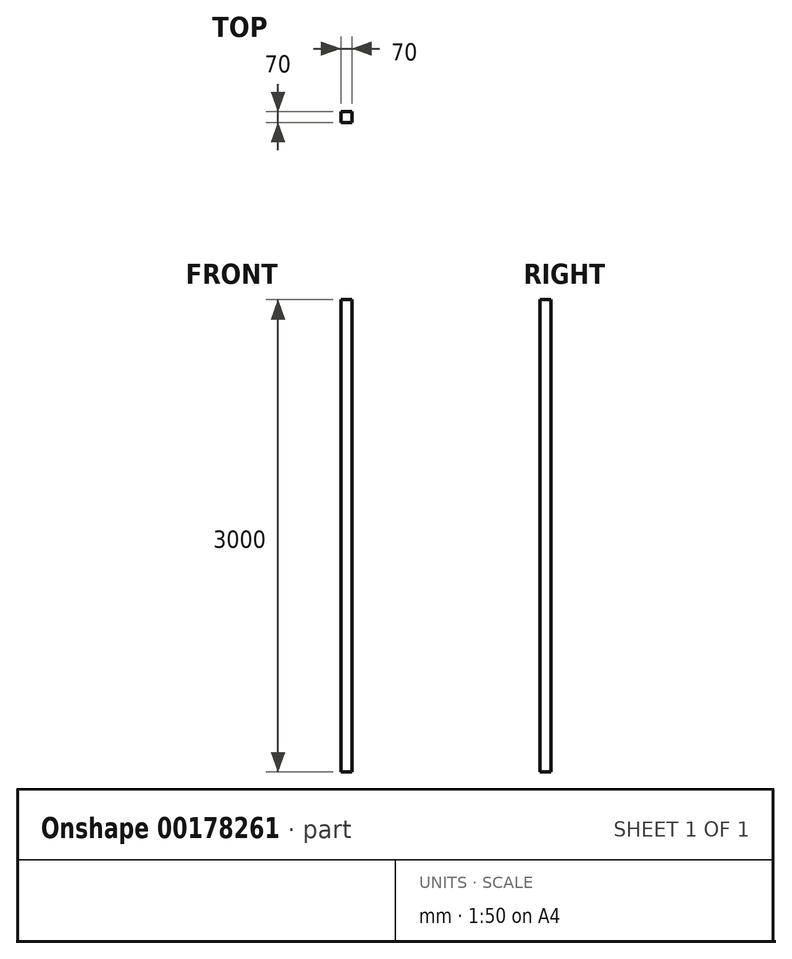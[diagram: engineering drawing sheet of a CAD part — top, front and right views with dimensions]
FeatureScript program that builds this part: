
annotation { "Feature Type Name" : "Feature", "Feature Type Description" : "" }
export const myFeature = defineFeature(function(context is Context, id is Id, definition is map)
    precondition{}
    {
        {
            var Q0;
            Q0=qCreatedBy(makeId("Top.planeOp"),FACE);
            var sketch = newSketch(context, id + "F0", { "sketchPlane" : qUnion([Q0])});
            skLineSegment(sketch, "E0.bottom", {"start": v(-35, -35) * mm, "end": v(35, -35) * mm});
            skLineSegment(sketch, "E0.top", {"start": v(-35, 35) * mm, "end": v(35, 35) * mm});
            skLineSegment(sketch, "E0.left", {"start": v(-35, -35) * mm, "end": v(-35, 35) * mm});
            skLineSegment(sketch, "E0.right", {"start": v(35, -35) * mm, "end": v(35, 35) * mm});
            skPoint(sketch, "E0.middle", {"position": v(0, 0) * mm});
            skSolve(sketch);
        }
        {
            var Q0;
            Q0 = qSketchRegion(id + "F0", true);
            extrude(context, id + "F1", {"entities" : qUnion([Q0]), "depth" : 3000 * mm});
        }
    });
